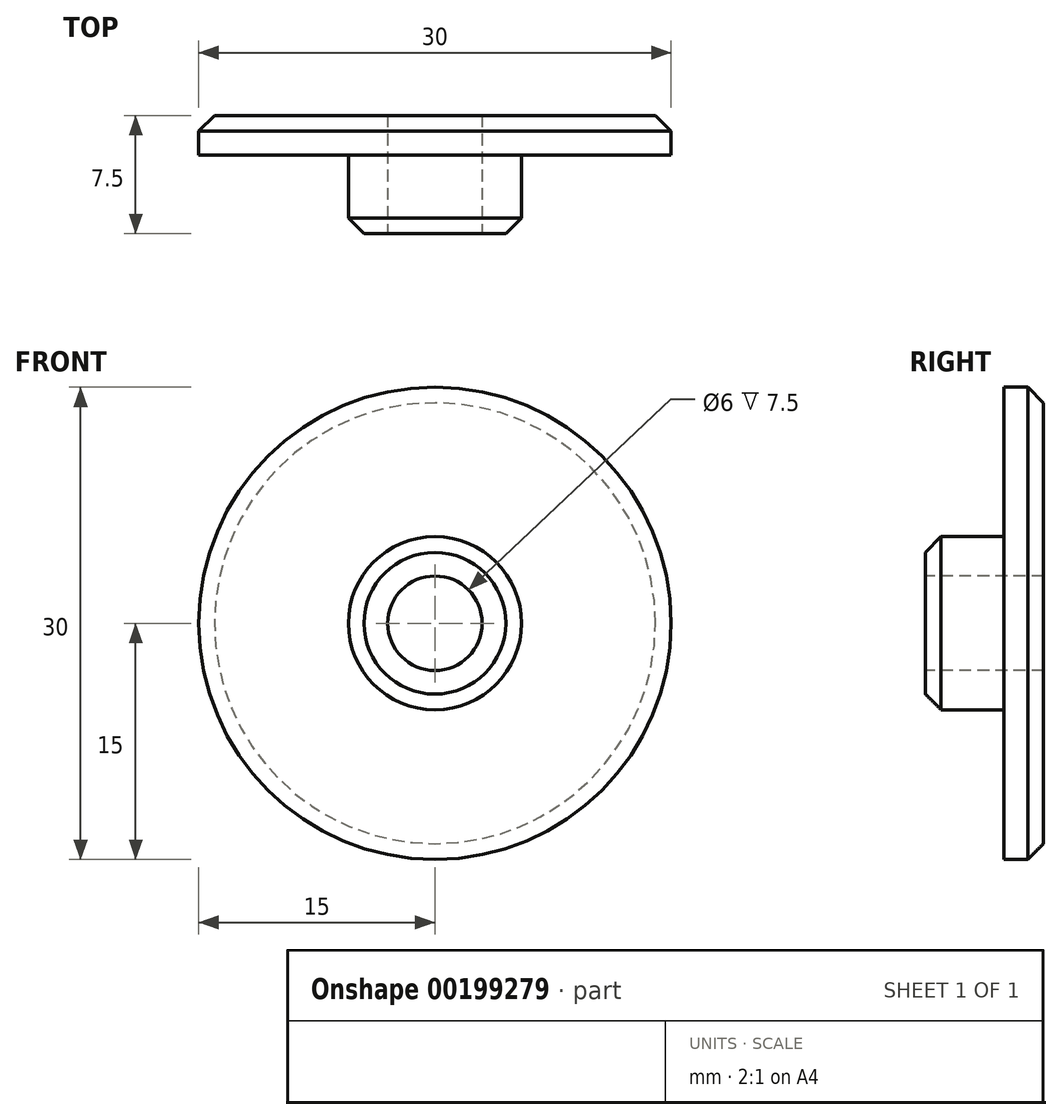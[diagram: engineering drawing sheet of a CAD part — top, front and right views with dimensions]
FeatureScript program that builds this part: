
annotation { "Feature Type Name" : "Feature", "Feature Type Description" : "" }
export const myFeature = defineFeature(function(context is Context, id is Id, definition is map)
    precondition{}
    {
        {
            var Q0;
            Q0=qCreatedBy(makeId("Front.planeOp"),FACE);
            var sketch = newSketch(context, id + "F0", { "sketchPlane" : qUnion([Q0])});
            skCircle(sketch, "E0", {"center": v(0, 0) * mm, "radius": 15 * mm});
            skSolve(sketch);
        }
        {
            var Q0;
            Q0=makeQuery(id+"F0.imprint","IMPRINT",FACE,{"disambiguationData":[TD([[makeQuery(id+"F0.imprint","IMPRINT",EDGE,{"derivedFrom":sQuery(id+"F0.wireOp",EDGE,"E0")}),1.0]])]});
            extrude(context, id + "F1", {"entities" : qUnion([Q0]), "depth" : 2.5 * mm});
        }
        {
            var Q0;
            Q0=makeQuery(id+"F1.opExtrude","CAP_FACE",FACE,{"disambiguationData":[OSD([sQuery(id+"F0.wireOp",EDGE,"E0")])],"isStart":false});
            var sketch = newSketch(context, id + "F2", { "sketchPlane" : qUnion([Q0])});
            skCircle(sketch, "E1", {"center": v(0, 0) * mm, "radius": 5.5 * mm});
            skSolve(sketch);
        }
        {
            var Q0;
            Q0 = qSketchRegion(id + "F2", true);
            extrude(context, id + "F3", {"entities" : qUnion([Q0]), "operationType" : NewBodyOperationType.ADD, "depth" : 5 * mm});
        }
        {
            var Q0;
            Q0=makeQuery(id+"F3.opExtrude","CAP_FACE",FACE,{"disambiguationData":[OSD([sQuery(id+"F2.wireOp",EDGE,"E1")])],"isStart":false});
            var sketch = newSketch(context, id + "F4", { "sketchPlane" : qUnion([Q0])});
            skCircle(sketch, "E2", {"center": v(0, 0) * mm, "radius": 3 * mm});
            skSolve(sketch);
        }
        {
            var Q0;
            Q0 = qSketchRegion(id + "F4", true);
            var Q1;
            Q1=sQuery(id+"F4.wireOp",EDGE,"E2");
            extrude(context, id + "F5", {"entities" : qUnion([Q0]), "operationType" : NewBodyOperationType.REMOVE, "surfaceEntities" : qUnion([Q1]), "oppositeDirection" : true, "depth" : 25 * mm});
        }
        {
            var Q0;
            Q0=makeQuery(id+"F3.opExtrude","CAP_EDGE",EDGE,{"disambiguationData":[OSD([sQuery(id+"F2.wireOp",EDGE,"E1")])],"isStart":false});
            var Q1;
            Q1=makeQuery(id+"F1.opExtrude","CAP_EDGE",EDGE,{"disambiguationData":[OSD([sQuery(id+"F0.wireOp",EDGE,"E0")])],"isStart":true});
            chamfer(context, id + "F6", {"entities" : qUnion([Q0, Q1]), "width" : 1 * mm, "tangentPropagation" : true});
        }
    });
